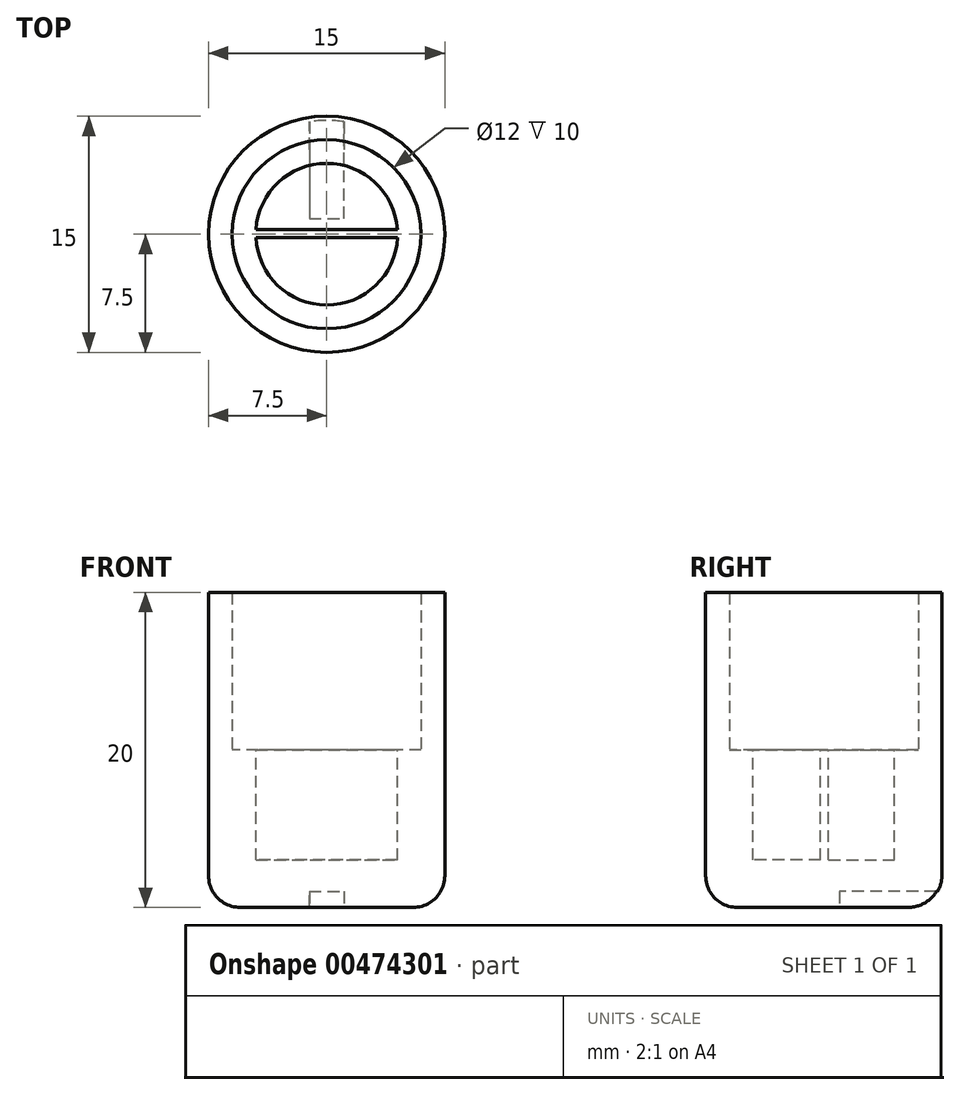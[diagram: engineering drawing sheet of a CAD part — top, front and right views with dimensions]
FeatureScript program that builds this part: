
annotation { "Feature Type Name" : "Feature", "Feature Type Description" : "" }
export const myFeature = defineFeature(function(context is Context, id is Id, definition is map)
    precondition{}
    {
        {
            var Q0;
            Q0=qCreatedBy(makeId("Top.planeOp"),FACE);
            var sketch = newSketch(context, id + "F0", { "sketchPlane" : qUnion([Q0])});
            skCircle(sketch, "E0", {"center": v(0, 0) * mm, "radius": 7.5 * mm});
            skSolve(sketch);
        }
        {
            var Q0;
            Q0=makeQuery(id+"F0.imprint","IMPRINT",FACE,{"disambiguationData":[TD([[makeQuery(id+"F0.imprint","IMPRINT",EDGE,{"derivedFrom":sQuery(id+"F0.wireOp",EDGE,"E0")}),1.0]])]});
            extrude(context, id + "F1", {"entities" : qUnion([Q0]), "depth" : 10 * mm});
        }
        {
            var Q0;
            Q0=makeQuery(id+"F1.opExtrude","CAP_FACE",FACE,{"disambiguationData":[OSD([sQuery(id+"F0.wireOp",EDGE,"E0")])],"isStart":false});
            var sketch = newSketch(context, id + "F2", { "sketchPlane" : qUnion([Q0])});
            skCircle(sketch, "E1.converted", {"center": v(0, 0) * mm, "radius": 6 * mm});
            skCircle(sketch, "E2", {"center": v(0, 0) * mm, "radius": 4.5 * mm});
            skCircle(sketch, "E3.0", {"center": v(0, 0) * mm, "radius": 5.5 * mm});
            skLineSegment(sketch, "E4", {"start": v(4.49, 0.3) * mm, "end": v(-4.49, 0.3) * mm});
            skLineSegment(sketch, "E5", {"start": v(4.5, -0.2) * mm, "end": v(-4.5, -0.2) * mm});
            skLineSegment(sketch, "E6", {"start": v(-3.67, 0.3) * mm, "end": v(-3.67, 4.1) * mm, "construction": true});
            skLineSegment(sketch, "E7", {"start": v(-3.78, -0.2) * mm, "end": v(-3.78, -4) * mm, "construction": true});
            skSolve(sketch);
        }
        {
            var Q0;
            {var subQ0=sQuery(id+"F2.wireOp",EDGE,"E4");Q0=makeQuery(id+"F2.imprint","IMPRINT",FACE,{"disambiguationData":[TD([[makeQuery(id+"F2.imprint","IMPRINT",EDGE,{"derivedFrom":subQ0}),-1.0]])]});}
            var Q1;
            {var subQ0=sQuery(id+"F2.wireOp",EDGE,"E5");Q1=makeQuery(id+"F2.imprint","IMPRINT",FACE,{"disambiguationData":[TD([[makeQuery(id+"F2.imprint","IMPRINT",EDGE,{"derivedFrom":subQ0}),1.0]])]});}
            extrude(context, id + "F3", {"entities" : qUnion([Q0, Q1]), "operationType" : NewBodyOperationType.REMOVE, "oppositeDirection" : true, "depth" : 7 * mm, "offsetDistance" : 25 * mm});
        }
        {
            var Q0;
            Q0=makeQuery(id+"F1.opExtrude","CAP_FACE",FACE,{"disambiguationData":[OSD([sQuery(id+"F0.wireOp",EDGE,"E0")])],"isStart":true});
            var sketch = newSketch(context, id + "F4", { "sketchPlane" : qUnion([Q0])});
            skLineSegment(sketch, "E8", {"start": v(0, -7.5) * mm, "end": v(0, 0) * mm, "construction": true});
            skLineSegment(sketch, "E9", {"start": v(-1.1, -7.42) * mm, "end": v(-1.1, -1) * mm});
            skLineSegment(sketch, "E10", {"start": v(-1.1, -1) * mm, "end": v(0, -1) * mm});
            skLineSegment(sketch, "E11", {"start": v(0, -1) * mm, "end": v(1.1, -1) * mm});
            skLineSegment(sketch, "E12", {"start": v(1.1, -1) * mm, "end": v(1.1, -7.42) * mm});
            skPoint(sketch, "E13.endSnap0", {"position": v(1.1, -4.2) * mm});
            skSolve(sketch);
        }
        {
            var Q0;
            {var subQ1=sQuery(id+"F4.wireOp",EDGE,"E9");Q0=makeQuery(id+"F4.imprint","IMPRINT",FACE,{"disambiguationData":[TD([[makeQuery(id+"F4.imprint","IMPRINT",EDGE,{"derivedFrom":subQ1}),-1.0]])]});}
            extrude(context, id + "F5", {"entities" : qUnion([Q0]), "operationType" : NewBodyOperationType.REMOVE, "oppositeDirection" : true, "depth" : 1 * mm});
        }
        {
            var Q0;
            Q0=makeQuery(id+"F1.opExtrude","CAP_EDGE",EDGE,{"disambiguationData":[OSD([sQuery(id+"F0.wireOp",EDGE,"E0")])],"isStart":true});
            fillet(context, id + "F6", {"entities" : qUnion([Q0]), "radius" : 2 * mm, "tangentPropagation" : true, "allowEdgeOverflow" : false});
        }
        {
            var Q0;
            Q0=makeQuery(id+"F2.imprint","IMPRINT",FACE,{"disambiguationData":[TD([[makeQuery(id+"F2.imprint","IMPRINT",EDGE,{"derivedFrom":sQuery(id+"F2.wireOp",EDGE,"E1.converted")}),-1.0]])]});
            extrude(context, id + "F7", {"entities" : qUnion([Q0]), "operationType" : NewBodyOperationType.ADD, "depth" : 5 * mm, "offsetDistance" : 25 * mm});
        }
        {
            var Q0;
            Q0=makeQuery(id+"F7.opExtrude","CAP_FACE",FACE,{"disambiguationData":[OSD([sQuery(id+"F0.wireOp",EDGE,"E0"),sQuery(id+"F2.wireOp",EDGE,"E1.converted")])],"isStart":false});
            extrude(context, id + "F8", {"entities" : qUnion([Q0]), "operationType" : NewBodyOperationType.ADD, "depth" : 5 * mm, "offsetDistance" : 25 * mm});
        }
    });
